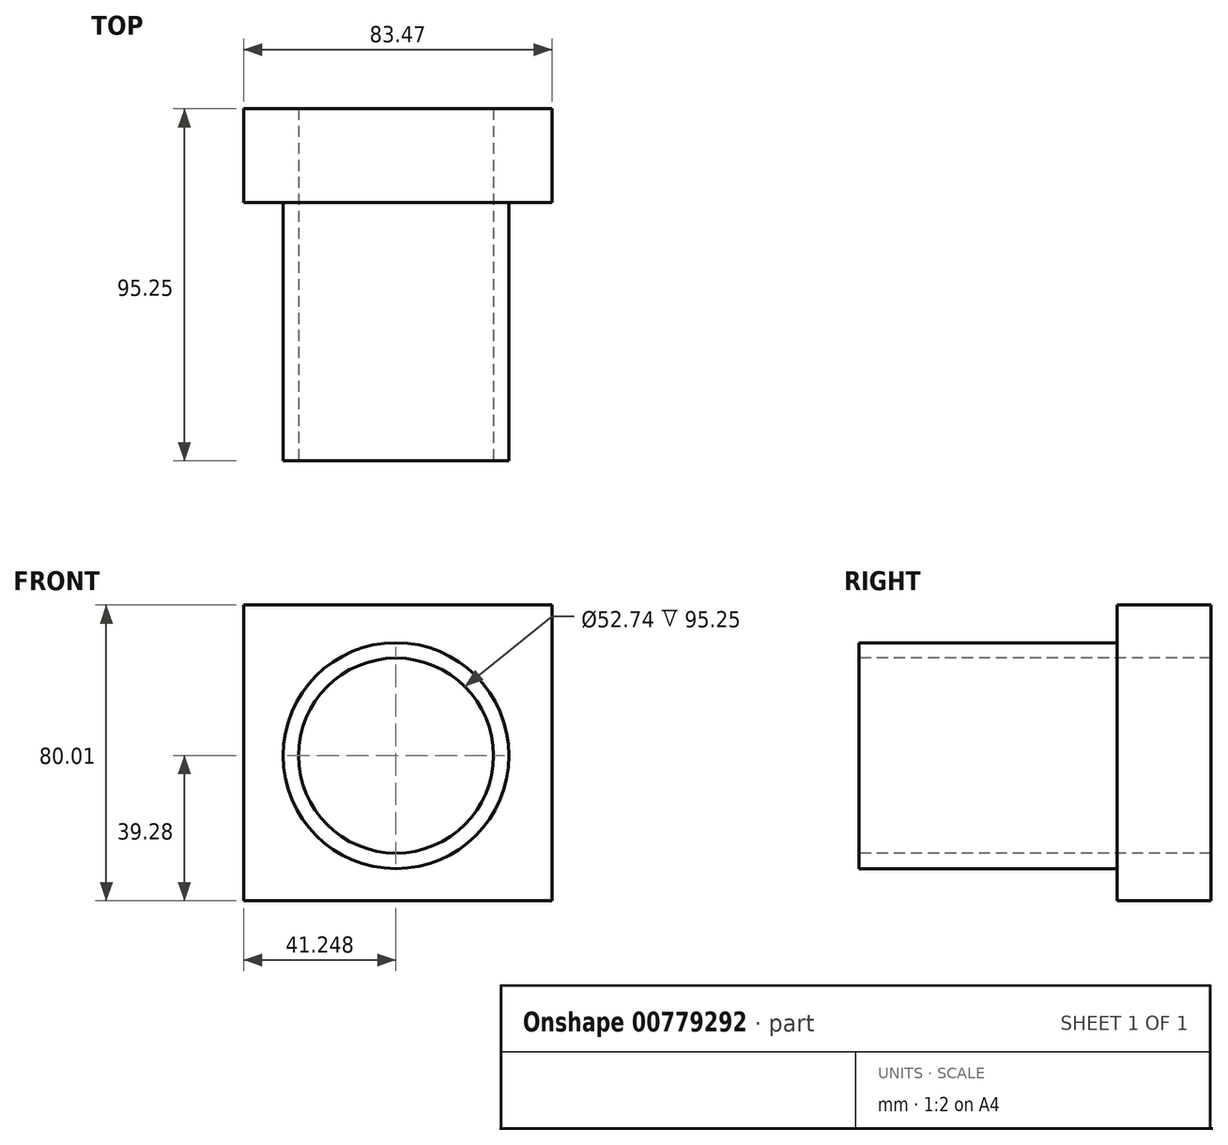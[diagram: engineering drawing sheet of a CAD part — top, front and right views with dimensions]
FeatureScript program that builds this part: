
annotation { "Feature Type Name" : "Feature", "Feature Type Description" : "" }
export const myFeature = defineFeature(function(context is Context, id is Id, definition is map)
    precondition{}
    {
        {
            var Q0;
            Q0=qCreatedBy(makeId("Front.planeOp"),FACE);
            var sketch = newSketch(context, id + "F0", { "sketchPlane" : qUnion([Q0])});
            skLineSegment(sketch, "E0.bottom", {"start": v(-31.23, 34.1) * mm, "end": v(52.24, 34.1) * mm});
            skLineSegment(sketch, "E0.top", {"start": v(-31.23, -45.9) * mm, "end": v(52.24, -45.9) * mm});
            skLineSegment(sketch, "E0.left", {"start": v(-31.23, 34.1) * mm, "end": v(-31.23, -45.9) * mm});
            skLineSegment(sketch, "E0.right", {"start": v(52.24, 34.1) * mm, "end": v(52.24, -45.9) * mm});
            skSolve(sketch);
        }
        {
            var Q0;
            Q0 = qSketchRegion(id + "F0", true);
            extrude(context, id + "F1", {"entities" : qUnion([Q0]), "depth" : 25.4 * mm, "offsetDistance" : 25.4 * mm});
        }
        {
            var Q0;
            Q0=makeQuery(id+"F1.opExtrude","CAP_FACE",FACE,{"disambiguationData":[OSD([sQuery(id+"F0.wireOp",EDGE,"E0.bottom"),sQuery(id+"F0.wireOp",EDGE,"E0.top"),sQuery(id+"F0.wireOp",EDGE,"E0.left"),sQuery(id+"F0.wireOp",EDGE,"E0.right")])],"isStart":false});
            var sketch = newSketch(context, id + "F2", { "sketchPlane" : qUnion([Q0])});
            skCircle(sketch, "E1", {"center": v(10.02, -6.63) * mm, "radius": 30.55 * mm});
            skSolve(sketch);
        }
        {
            var Q0;
            Q0 = qSketchRegion(id + "F2", true);
            extrude(context, id + "F3", {"entities" : qUnion([Q0]), "operationType" : NewBodyOperationType.ADD, "depth" : 69.85 * mm, "offsetDistance" : 25.4 * mm});
        }
        {
            var Q0;
            Q0=makeQuery(id+"F3.opExtrude","CAP_FACE",FACE,{"disambiguationData":[OSD([sQuery(id+"F2.wireOp",EDGE,"E1")])],"isStart":false});
            var sketch = newSketch(context, id + "F4", { "sketchPlane" : qUnion([Q0])});
            skCircle(sketch, "E2", {"center": v(10.02, -6.63) * mm, "radius": 26.37 * mm});
            skSolve(sketch);
        }
        {
            var Q0;
            Q0 = qSketchRegion(id + "F4", true);
            extrude(context, id + "F5", {"entities" : qUnion([Q0]), "operationType" : NewBodyOperationType.REMOVE, "oppositeDirection" : true, "depth" : 133.6 * mm, "offsetDistance" : 25.4 * mm});
        }
    });
